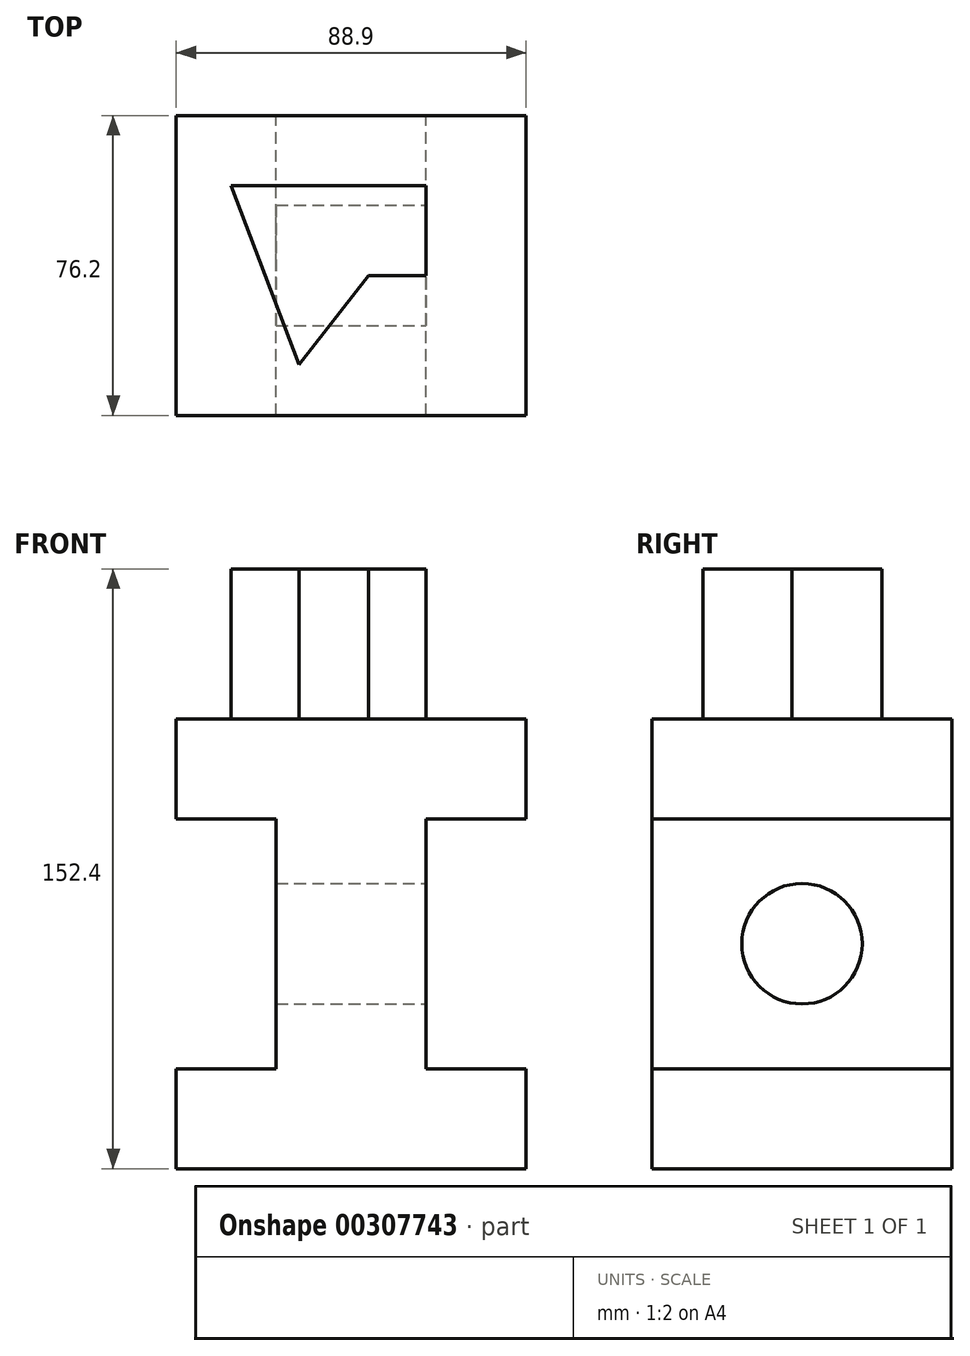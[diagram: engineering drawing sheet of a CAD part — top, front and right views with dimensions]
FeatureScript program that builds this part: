
annotation { "Feature Type Name" : "Feature", "Feature Type Description" : "" }
export const myFeature = defineFeature(function(context is Context, id is Id, definition is map)
    precondition{}
    {
        {
            var Q0;
            Q0=qCreatedBy(makeId("Front.planeOp"),FACE);
            var sketch = newSketch(context, id + "F0", { "sketchPlane" : qUnion([Q0])});
            skLineSegment(sketch, "E0", {"start": v(40.03, -52.18) * mm, "end": v(40.03, -26.78) * mm});
            skLineSegment(sketch, "E1", {"start": v(40.03, -26.78) * mm, "end": v(14.63, -26.78) * mm});
            skLineSegment(sketch, "E2", {"start": v(14.63, -26.78) * mm, "end": v(14.63, 36.72) * mm});
            skLineSegment(sketch, "E3", {"start": v(14.63, 36.72) * mm, "end": v(40.03, 36.72) * mm});
            skLineSegment(sketch, "E4", {"start": v(40.03, 36.72) * mm, "end": v(40.03, 62.12) * mm});
            skLineSegment(sketch, "E5", {"start": v(40.03, 62.12) * mm, "end": v(-48.87, 62.12) * mm});
            skLineSegment(sketch, "E6", {"start": v(-48.87, 62.12) * mm, "end": v(-48.87, 36.72) * mm});
            skLineSegment(sketch, "E7", {"start": v(-48.87, 36.72) * mm, "end": v(-23.47, 36.72) * mm});
            skLineSegment(sketch, "E8", {"start": v(-23.47, 36.72) * mm, "end": v(-23.47, -26.78) * mm});
            skLineSegment(sketch, "E9", {"start": v(-23.47, -26.78) * mm, "end": v(-48.87, -26.78) * mm});
            skLineSegment(sketch, "E10", {"start": v(-48.87, -26.78) * mm, "end": v(-48.87, -52.18) * mm});
            skLineSegment(sketch, "E11", {"start": v(-48.87, -52.18) * mm, "end": v(40.03, -52.18) * mm});
            skSolve(sketch);
        }
        {
            var Q0;
            Q0=makeQuery(id+"F0.imprint","IMPRINT",FACE,{"disambiguationData":[TD([[makeQuery(id+"F0.imprint","IMPRINT",EDGE,{"derivedFrom":sQuery(id+"F0.wireOp",EDGE,"LAcm8mc8-IbR6-HwYL-lCDK-3mCIDZ61TpqG")}),1.0]])]});
            var Q1;
            Q1=makeQuery(id+"F0.imprint","IMPRINT",FACE,{"disambiguationData":[TD([[makeQuery(id+"F0.imprint","IMPRINT",EDGE,{"derivedFrom":sQuery(id+"F0.wireOp",EDGE,"E0")}),1.0]])]});
            extrude(context, id + "F1", {"entities" : qUnion([Q0, Q1]), "depth" : 76.2 * mm});
        }
        {
            var Q0;
            Q0=makeQuery(id+"F1.opExtrude","SWEPT_FACE",FACE,{"disambiguationData":[OSD([sQuery(id+"F0.wireOp",EDGE,"E2")])]});
            var sketch = newSketch(context, id + "F2", { "sketchPlane" : qUnion([Q0])});
            skCircle(sketch, "E12", {"center": v(-38.1, 4.97) * mm, "radius": 15.3 * mm});
            skPoint(sketch, "E12.centerSnap0", {"position": v(-38.1, 36.72) * mm});
            skPoint(sketch, "E12.centerSnap1", {"position": v(-76.2, 4.97) * mm});
            skSolve(sketch);
        }
        {
            var Q0;
            Q0=makeQuery(id+"F2.imprint","IMPRINT",FACE,{"disambiguationData":[TD([[makeQuery(id+"F2.imprint","IMPRINT",EDGE,{"derivedFrom":sQuery(id+"F2.wireOp",EDGE,"E12")}),1.0]])]});
            extrude(context, id + "F3", {"entities" : qUnion([Q0]), "operationType" : NewBodyOperationType.REMOVE, "endBound" : BoundingType.THROUGH_ALL, "oppositeDirection" : true, "depth" : 25.4 * mm});
        }
        {
            var Q0;
            Q0=makeQuery(id+"F1.opExtrude","SWEPT_FACE",FACE,{"disambiguationData":[OSD([sQuery(id+"F0.wireOp",EDGE,"E5")])]});
            var sketch = newSketch(context, id + "F4", { "sketchPlane" : qUnion([Q0])});
            skLineSegment(sketch, "E13", {"start": v(0, -40.7) * mm, "end": v(14.55, -40.7) * mm});
            skLineSegment(sketch, "E14", {"start": v(14.55, -40.7) * mm, "end": v(14.55, -17.8) * mm});
            skLineSegment(sketch, "E15", {"start": v(14.55, -17.8) * mm, "end": v(-34.98, -17.8) * mm});
            skLineSegment(sketch, "E16", {"start": v(-34.98, -17.8) * mm, "end": v(-17.64, -63.3) * mm});
            skLineSegment(sketch, "E17", {"start": v(-17.64, -63.3) * mm, "end": v(0, -40.7) * mm});
            skSolve(sketch);
        }
        {
            var Q0;
            Q0=makeQuery(id+"F4.imprint","IMPRINT",FACE,{"disambiguationData":[TD([[makeQuery(id+"F4.imprint","IMPRINT",EDGE,{"derivedFrom":sQuery(id+"F4.wireOp",EDGE,"E13")}),1.0]])]});
            extrude(context, id + "F5", {"entities" : qUnion([Q0]), "operationType" : NewBodyOperationType.ADD, "depth" : 38.1 * mm});
        }
    });
